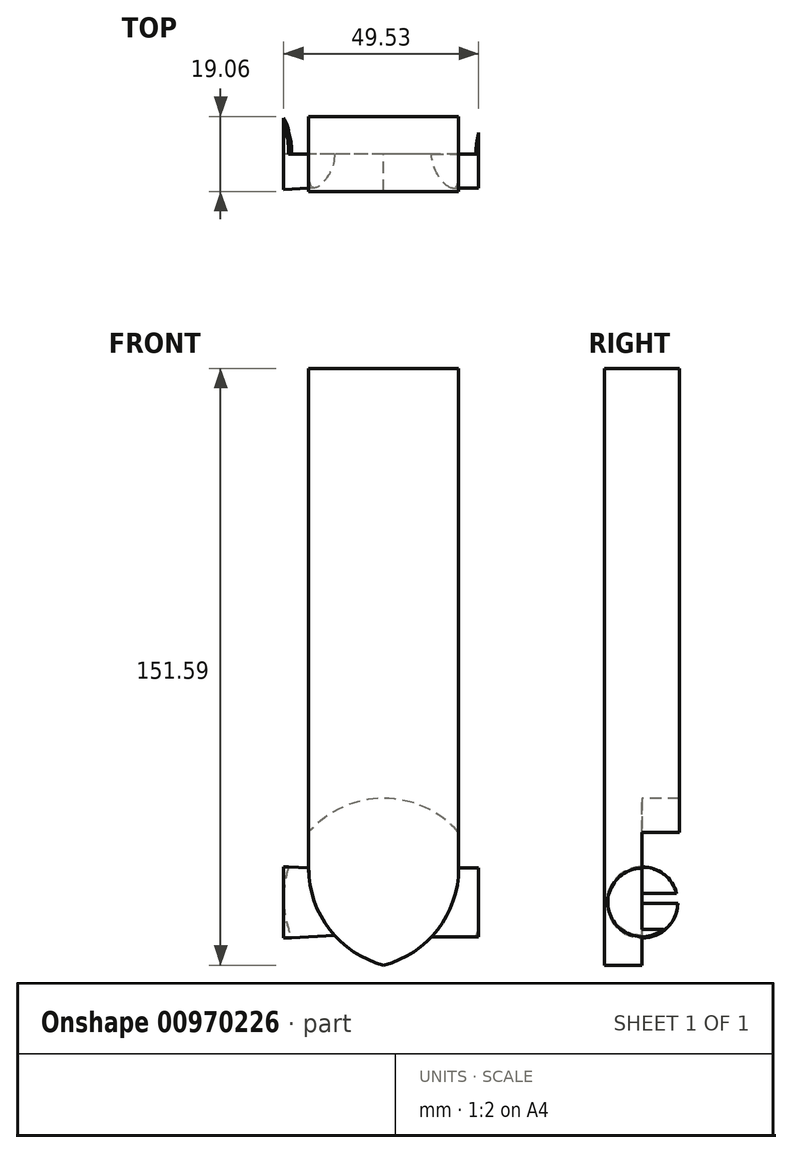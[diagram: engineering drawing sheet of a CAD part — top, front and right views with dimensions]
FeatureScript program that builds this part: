
annotation { "Feature Type Name" : "Feature", "Feature Type Description" : "" }
export const myFeature = defineFeature(function(context is Context, id is Id, definition is map)
    precondition{}
    {
        {
            var Q0;
            Q0=qCreatedBy(makeId("Front.planeOp"),FACE);
            var sketch = newSketch(context, id + "F0", { "sketchPlane" : qUnion([Q0])});
            skLineSegment(sketch, "E0", {"start": v(0, 76.2) * mm, "end": v(0, -76.2) * mm});
            skLineSegment(sketch, "E1", {"start": v(0, -76.2) * mm, "end": v(38.1, -76.2) * mm});
            skLineSegment(sketch, "E2", {"start": v(38.1, -76.2) * mm, "end": v(38.1, 76.2) * mm});
            skLineSegment(sketch, "E3", {"start": v(38.1, 76.2) * mm, "end": v(0, 76.2) * mm});
            skPoint(sketch, "E4.centerSnap0", {"position": v(0, 0) * mm});
            skLineSegment(sketch, "E5", {"start": v(38.1, 0) * mm, "end": v(0, 0) * mm});
            skLineSegment(sketch, "E6", {"start": v(0, 0) * mm, "end": v(0, 0) * mm});
            skPoint(sketch, "E6.endSnap0", {"position": v(19.05, 0) * mm});
            skSolve(sketch);
        }
        {
            var Q0;
            Q0=makeQuery(id+"F0.imprint","IMPRINT",FACE,{"disambiguationData":[TD([[makeQuery(id+"F0.imprint","IMPRINT",EDGE,{"derivedFrom":sQuery(id+"F0.wireOp",EDGE,"E0")}),1.0]])]});
            var Q1;
            {var subQ1=sQuery(id+"F0.wireOp",EDGE,"E1");Q1=makeQuery(id+"F0.imprint","IMPRINT",FACE,{"disambiguationData":[TD([[makeQuery(id+"F0.imprint","IMPRINT",EDGE,{"derivedFrom":subQ1}),1.0]])]});}
            extrude(context, id + "F1", {"entities" : qUnion([Q0, Q1]), "endBound" : BoundingType.SYMMETRIC, "depth" : 19.05 * mm, "offsetDistance" : 25.4 * mm});
        }
        {
            var Q0;
            Q0=qCreatedBy(makeId("Right.planeOp"),FACE);
            var sketch = newSketch(context, id + "F2", { "sketchPlane" : qUnion([Q0])});
            skCircle(sketch, "E7", {"center": v(0, -59.46) * mm, "radius": 8.72 * mm});
            skSolve(sketch);
        }
        {
            var Q0;
            Q0 = qSketchRegion(id + "F2", true);
            extrude(context, id + "F3", {"entities" : qUnion([Q0]), "operationType" : NewBodyOperationType.ADD, "oppositeDirection" : true, "depth" : 6.35 * mm, "offsetDistance" : 25.4 * mm, "hasDraft" : true, "draftAngle" : 3 * degree, "hasSecondDirection" : true, "secondDirectionOppositeDirection" : false, "secondDirectionDepth" : 43.18 * mm});
        }
        {
            var Q0;
            Q0=makeQuery(id+"F1.opExtrude","SWEPT_EDGE",EDGE,{"disambiguationData":[OSD([sQuery(id+"F0.wireOp",EDGE,"E1"),sQuery(id+"F0.wireOp",EDGE,"E2")])]});
            var Q1;
            Q1=makeQuery(id+"F1.opExtrude","SWEPT_EDGE",EDGE,{"disambiguationData":[OSD([sQuery(id+"F0.wireOp",EDGE,"E0"),sQuery(id+"F0.wireOp",EDGE,"E1")])]});
            fillet(context, id + "F4", {"entities" : qUnion([Q0, Q1]), "radius" : 25.4 * mm, "tangentPropagation" : true, "allowEdgeOverflow" : false});
        }
        {
            var Q0;
            Q0=qCreatedBy(makeId("Front.planeOp"),FACE);
            var sketch = newSketch(context, id + "F5", { "sketchPlane" : qUnion([Q0])});
            skCircle(sketch, "E8", {"center": v(19.02, -58.42) * mm, "radius": 17.04 * mm});
            skSolve(sketch);
        }
        {
            var Q0;
            Q0=sQuery(id+"F5.wireOp",VERTEX,"E8.center");
            var Q1;
            Q1=makeQuery(id+"F1.opExtrude","SWEPT_BODY",BODY,{"disambiguationData":[OSD([sQuery(id+"F0.wireOp",EDGE,"E0"),sQuery(id+"F0.wireOp",EDGE,"E1"),sQuery(id+"F0.wireOp",EDGE,"E2"),sQuery(id+"F0.wireOp",EDGE,"E3")])]});
            hole(context, id + "F6", {"style" : HoleStyle.C_BORE, "endStyle" : HoleEndStyle.THROUGH, "holeDiameter" : 25.4 * mm, "cBoreDiameter" : 50.8 * mm, "cBoreDepth" : 50.8 * mm, "majorDiameter" : 6.35 * mm, "isTappedThrough" : true, "tappedDepth" : 12.7 * mm, "tapClearance" : 3, "startFromSketch" : true, "locations" : qUnion([Q0]), "scope" : qUnion([Q1])});
        }
    });
